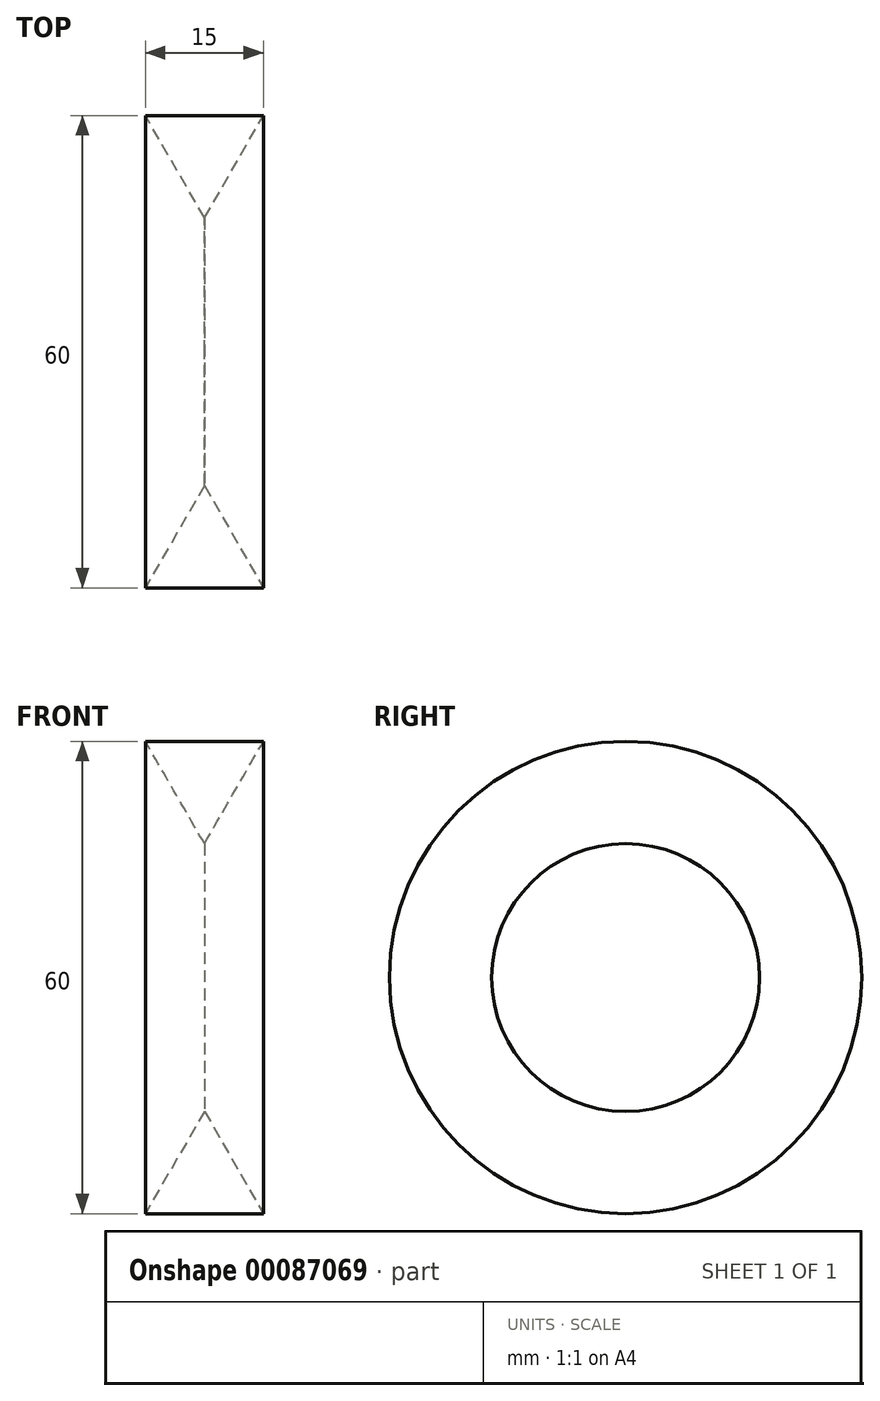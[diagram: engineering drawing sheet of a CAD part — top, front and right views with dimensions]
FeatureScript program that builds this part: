
annotation { "Feature Type Name" : "Feature", "Feature Type Description" : "" }
export const myFeature = defineFeature(function(context is Context, id is Id, definition is map)
    precondition{}
    {
        {
            var Q0;
            Q0=qCreatedBy(makeId("Front.planeOp"),FACE);
            var sketch = newSketch(context, id + "F0", { "sketchPlane" : qUnion([Q0])});
            skLineSegment(sketch, "E0", {"start": v(-7.5, 30) * mm, "end": v(0, 17) * mm});
            skLineSegment(sketch, "E1", {"start": v(0, 17) * mm, "end": v(7.5, 30) * mm});
            skLineSegment(sketch, "E2", {"start": v(7.5, 30) * mm, "end": v(-7.5, 30) * mm});
            skLineSegment(sketch, "E3", {"start": v(0, 17) * mm, "end": v(0, 0) * mm, "construction": true});
            skLineSegment(sketch, "E4", {"start": v(0, 17) * mm, "end": v(0, 30) * mm, "construction": true});
            skLineSegment(sketch, "E5", {"start": v(0, 0) * mm, "end": v(17, 0) * mm, "construction": true});
            skLineSegment(sketch, "E6", {"start": v(0, 23.5) * mm, "end": v(3.75, 23.5) * mm, "construction": true});
            skSolve(sketch);
        }
        {
            var Q0;
            Q0 = qSketchRegion(id + "F0", true);
            var Q1;
            Q1=sQuery(id+"F0.wireOp",EDGE,"E5");
            revolve(context, id + "F1", {"entities" : qUnion([Q0]), "axis" : qUnion([Q1]), "revolveType" : RevolveType.FULL});
        }
    });
